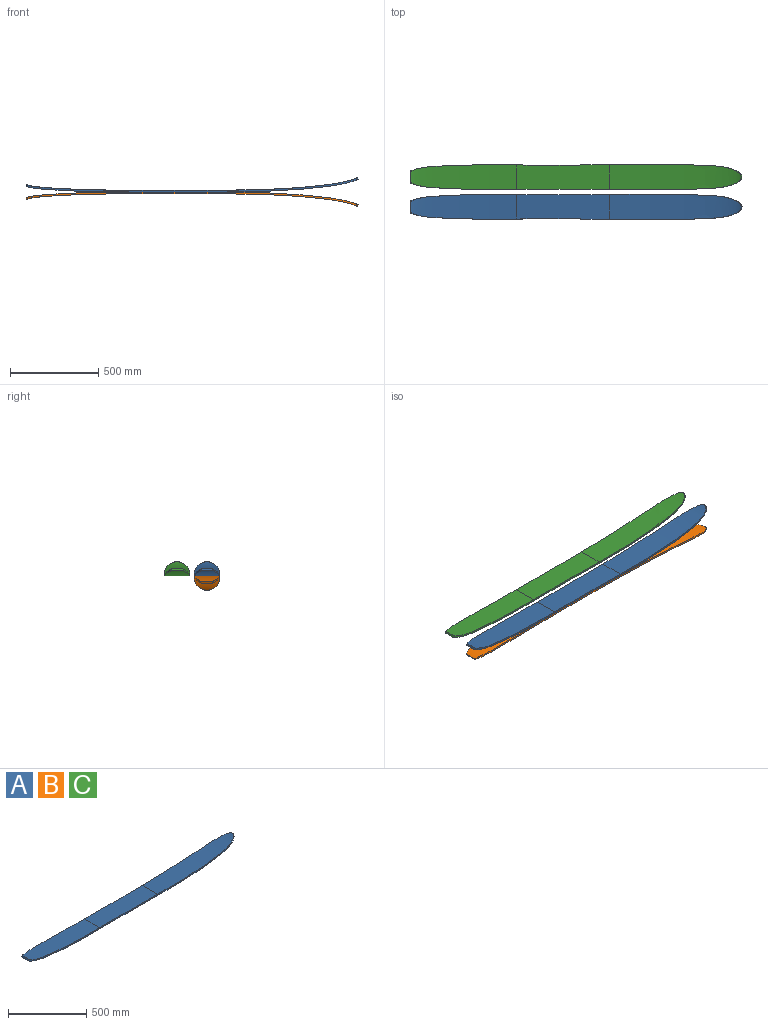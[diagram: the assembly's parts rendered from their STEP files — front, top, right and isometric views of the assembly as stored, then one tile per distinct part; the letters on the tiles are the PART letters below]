
ASSEMBLY  parts=3 mates=1
PART A: 22 faces, bbox 1880x144.1x81.7 mm
  f0: bspline ~117.9x25.02mm, area 1202mm2, adj f1,f15,f16,f19
  f1: bspline ~11.24x9.15mm, area 113.5mm2, adj f0,f2,f16,f19
  f2: plane 51.95x8.79mm, normal (-0.88,0,0.48), area 519.5mm2, adj f1,f3,f16,f19
  f3: bspline ~11.24x9.15mm, area 113.5mm2, adj f2,f4,f16,f19
  f4: bspline ~117.9x25.02mm, area 1202mm2, adj f3,f5,f16,f19
  f5: bspline ~322.12x22.61mm, area 3221.8mm2, adj f4,f6,f16,f19
  f6: bspline ~159.14x11.24mm, area 1590.7mm2, adj f5,f7,f16,f19
  f7: cylinder r=44959.61mm len=525.79mm, axis (0,0,1), area 5257.9mm2, adj f6,f8,f17,f20
  f8: bspline ~232.01x14.3mm, area 2318.8mm2, adj f7,f9,f18,f21
  f9: bspline ~354.19x38.18mm, area 3547.2mm2, adj f8,f10,f18,f21
  f10: bspline ~165.63x128.06mm, area 3783.5mm2, adj f9,f11,f18,f21
  f11: bspline ~354.19x38.18mm, area 3547.2mm2, adj f10,f12,f18,f21
  f12: bspline ~232.01x14.3mm, area 2318.8mm2, adj f11,f13,f18,f21
  f13: cylinder r=44959.61mm len=525.79mm, axis (0,0,1), area 5257.9mm2, adj f12,f14,f17,f20
  f14: bspline ~159.14x11.24mm, area 1590.7mm2, adj f13,f15,f16,f19
  f15: bspline ~322.12x22.61mm, area 3221.8mm2, adj f0,f14,f16,f19
  f16: extruded ~599.45x139mm, area 76863.4mm2, adj f0,f1,f2,f3,f4,f5,f6,f14
  f17: plane 525.79x138.49mm, normal (0,0,1), area 71836.9mm2, adj f7,f13,f16,f18
  f18: extruded ~745.02x143.15mm, area 96884.7mm2, adj f8,f9,f10,f11,f12,f17
  f19: extruded ~604.21x139mm, area 77263.7mm2, adj f0,f1,f2,f3,f4,f5,f6,f14
  f20: plane 525.79x138.49mm, normal (0,0,-1), area 71836.9mm2, adj f7,f13,f19,f21
  f21: extruded ~750.02x143.15mm, area 97186mm2, adj f8,f9,f10,f11,f12,f20
PART B: same geometry as A
PART C: same geometry as A
PLACE A t=(-197.92,-396.4,164.84)mm
PLACE B rot(axis=(1,0,0),180deg) t=(-197.92,-396.4,-15.16)mm
PLACE C t=(-197.95,-227.29,165.16)mm
MATE fastened B.f20 <-> A.f20  axis (0,0,1) through (-760.28,-396.4,74.84)mm
